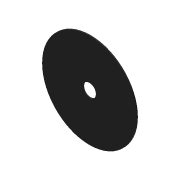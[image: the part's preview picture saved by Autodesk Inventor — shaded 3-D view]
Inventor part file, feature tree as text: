
AUTODESK INVENTOR PART (.ipt)
format: ipt  version: 2016 (Build 200138000, 138)  size: 80,384 bytes
history: native  units: in
note: dims shown in document units (in); Inventor stores cm internally (conversion verified against a paired STEP export)
features: extrude x2, sketch x2, other x1
ambient origin geometry x8: Origin, YZ Plane, XZ Plane, XY Plane, X Axis, Y Axis, Z Axis, Center Point
bodies: Solid1 (feature_tree)
feature tree (5):
  other  "skeleton.ipt"
  extrude  "Extrusion1"  Depth=0.3937in
  extrude  "Extrusion2"  Depth=0.3937in
  sketch  "Sketch1"  dims[d0=0.3937in d1=5.9055in]
  sketch  "Sketch2"  dims[d2=0.0787in d3=0.0in d4=0.8661in d5=0.3937in d6=0.0in]
